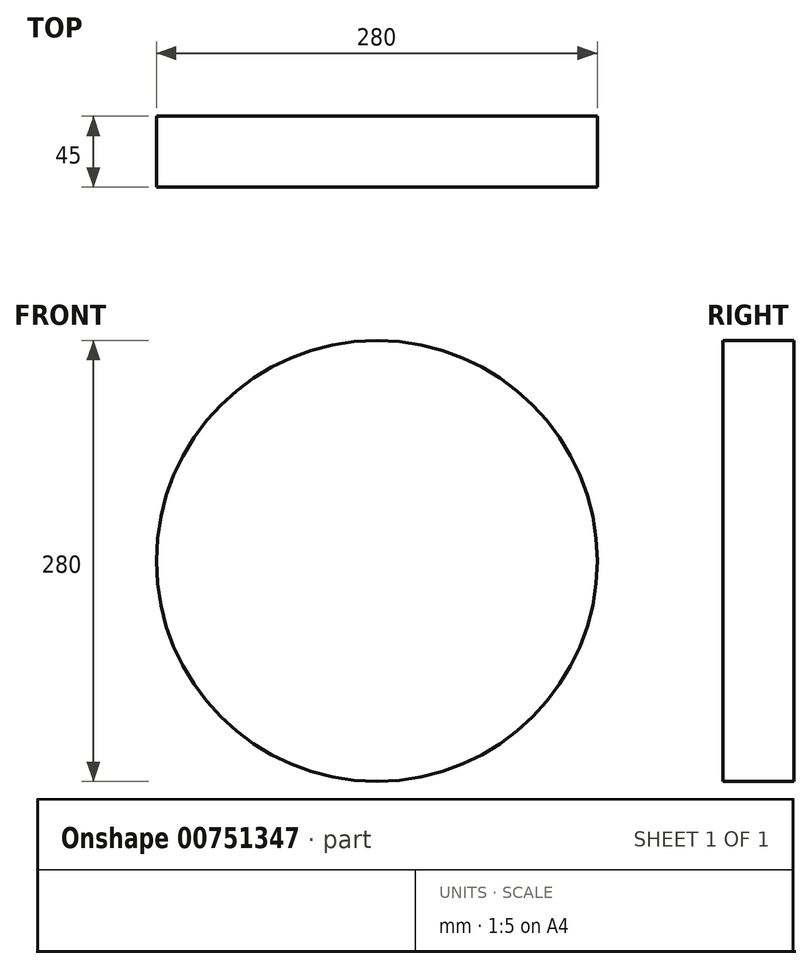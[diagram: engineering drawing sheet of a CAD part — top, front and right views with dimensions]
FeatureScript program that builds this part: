
annotation { "Feature Type Name" : "Feature", "Feature Type Description" : "" }
export const myFeature = defineFeature(function(context is Context, id is Id, definition is map)
    precondition{}
    {
        {
            var Q0;
            Q0=qCreatedBy(makeId("Front.planeOp"),FACE);
            var sketch = newSketch(context, id + "F0", { "sketchPlane" : qUnion([Q0])});
            skCircle(sketch, "E0", {"center": v(0, 0) * mm, "radius": 140 * mm});
            skSolve(sketch);
        }
        {
            var Q0;
            Q0 = qSketchRegion(id + "F0", true);
            extrude(context, id + "F1", {"entities" : qUnion([Q0]), "depth" : 45 * mm, "offsetDistance" : 25 * mm});
        }
    });
